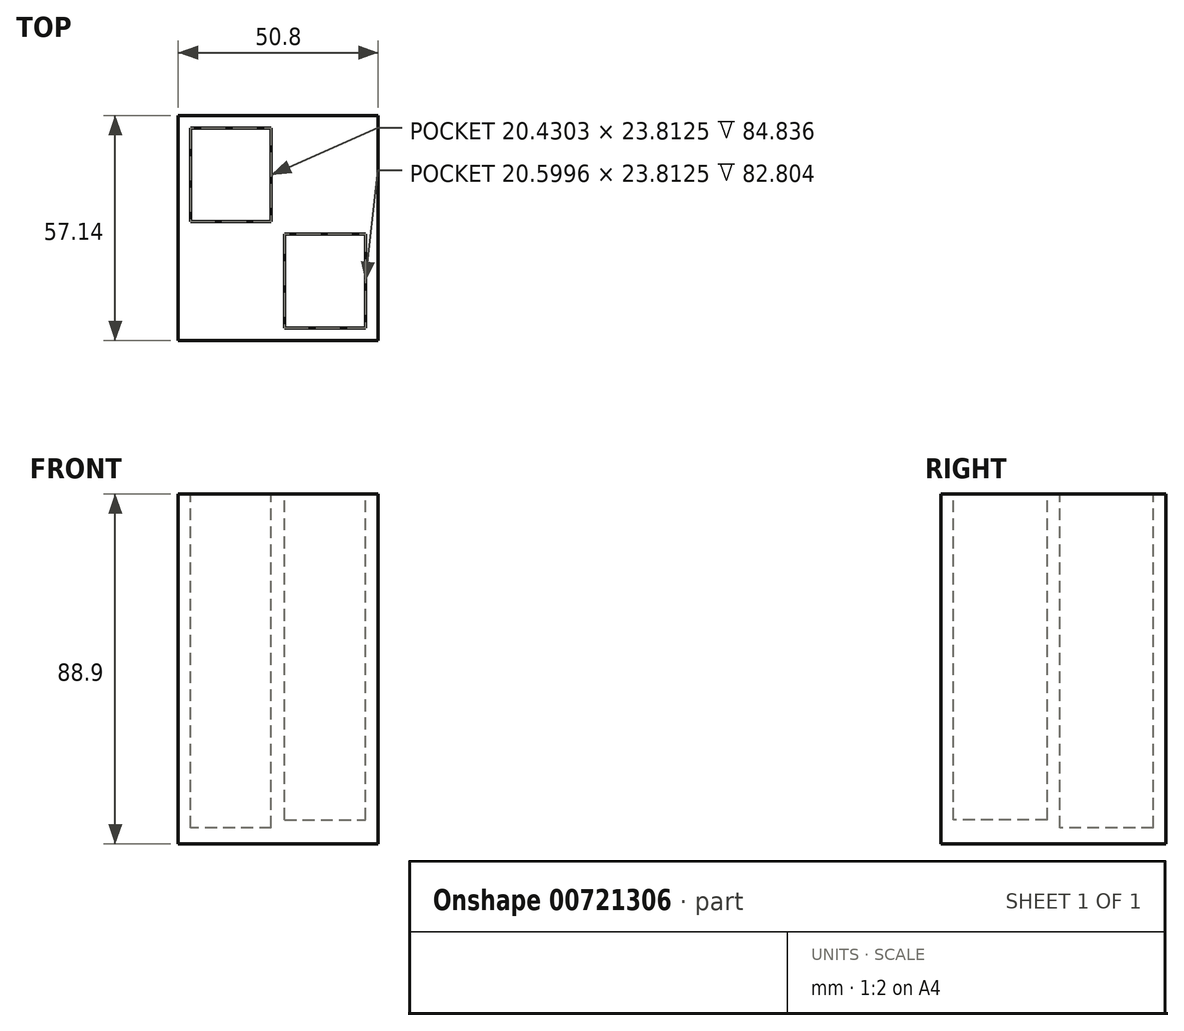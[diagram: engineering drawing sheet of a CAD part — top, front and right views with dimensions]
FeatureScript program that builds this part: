
annotation { "Feature Type Name" : "Feature", "Feature Type Description" : "" }
export const myFeature = defineFeature(function(context is Context, id is Id, definition is map)
    precondition{}
    {
        {
            var Q0;
            Q0=qCreatedBy(makeId("Top.planeOp"),FACE);
            var sketch = newSketch(context, id + "F0", { "sketchPlane" : qUnion([Q0])});
            skLineSegment(sketch, "E0.bottom", {"start": v(-25.4, 28.58) * mm, "end": v(25.4, 28.58) * mm});
            skLineSegment(sketch, "E0.top", {"start": v(-25.4, -28.58) * mm, "end": v(25.4, -28.58) * mm});
            skLineSegment(sketch, "E0.left", {"start": v(-25.4, 28.58) * mm, "end": v(-25.4, -28.58) * mm});
            skLineSegment(sketch, "E0.right", {"start": v(25.4, 28.58) * mm, "end": v(25.4, -28.58) * mm});
            skPoint(sketch, "E0.middle", {"position": v(0, 0) * mm});
            skSolve(sketch);
        }
        {
            var Q0;
            Q0 = qSketchRegion(id + "F0", true);
            extrude(context, id + "F1", {"entities" : qUnion([Q0]), "depth" : 88.9 * mm, "offsetDistance" : 25.4 * mm});
        }
        {
            var Q0;
            Q0=makeQuery(id+"F1.opExtrude","CAP_FACE",FACE,{"disambiguationData":[OSD([sQuery(id+"F0.wireOp",EDGE,"E0.bottom"),sQuery(id+"F0.wireOp",EDGE,"E0.top"),sQuery(id+"F0.wireOp",EDGE,"E0.left"),sQuery(id+"F0.wireOp",EDGE,"E0.right")])],"isStart":false});
            var sketch = newSketch(context, id + "F2", { "sketchPlane" : qUnion([Q0])});
            skLineSegment(sketch, "E1.0", {"start": v(-22.22, 25.4) * mm, "end": v(-22.23, 1.59) * mm});
            skLineSegment(sketch, "E1.1", {"start": v(22.23, 25.4) * mm, "end": v(-22.22, 25.4) * mm});
            skLineSegment(sketch, "E1.2", {"start": v(22.22, -25.4) * mm, "end": v(22.23, -1.59) * mm});
            skLineSegment(sketch, "E1.3", {"start": v(-22.23, -25.4) * mm, "end": v(22.22, -25.4) * mm});
            skLineSegment(sketch, "E2.0", {"start": v(-22.23, -1.59) * mm, "end": v(22.22, -1.59) * mm});
            skLineSegment(sketch, "E3", {"start": v(-22.23, 1.59) * mm, "end": v(22.23, 1.59) * mm});
            skPoint(sketch, "E4.orphan", {"position": v(22.23, 0) * mm});
            skLineSegment(sketch, "E5.trimOffspring", {"start": v(22.23, 1.59) * mm, "end": v(22.23, 25.4) * mm});
            skPoint(sketch, "E6.start.orphan", {"position": v(-22.23, 0) * mm});
            skLineSegment(sketch, "E7.trimOffspring", {"start": v(-22.23, -1.59) * mm, "end": v(-22.23, -25.4) * mm});
            skPoint(sketch, "E8.start.orphan", {"position": v(0, 25.4) * mm});
            skPoint(sketch, "E9.trimOffspring.end.orphan", {"position": v(0, -25.4) * mm});
            skSolve(sketch);
        }
        {
            var Q0;
            {var subQ0=sQuery(id+"F2.wireOp",EDGE,"E1.0");Q0=makeQuery(id+"F2.imprint","IMPRINT",FACE,{"disambiguationData":[TD([[makeQuery(id+"F2.imprint","IMPRINT",EDGE,{"derivedFrom":subQ0}),1.0]])]});}
            var sketch = newSketch(context, id + "F3", { "sketchPlane" : qUnion([Q0])});
            skLineSegment(sketch, "E10", {"start": v(-1.8, 25.41) * mm, "end": v(-1.8, 1.53) * mm});
            skLineSegment(sketch, "E11", {"start": v(1.44, 25.41) * mm, "end": v(1.44, 1.72) * mm});
            skSolve(sketch);
        }
        {
            var Q0;
            Q0=makeQuery(id+"F2.imprint","IMPRINT",FACE,{"disambiguationData":[TD([[makeQuery(id+"F2.imprint","IMPRINT",EDGE,{"derivedFrom":sQuery(id+"F2.wireOp",EDGE,"E1.2")}),1.0]])]});
            var sketch = newSketch(context, id + "F4", { "sketchPlane" : qUnion([Q0])});
            skLineSegment(sketch, "E12", {"start": v(-1.79, -1.63) * mm, "end": v(-1.79, -25.14) * mm});
            skPoint(sketch, "E13.start.orphan", {"position": v(0, -1.63) * mm});
            skLineSegment(sketch, "E14", {"start": v(1.63, -1.44) * mm, "end": v(1.63, -25.71) * mm});
            skSolve(sketch);
        }
        {
            var Q0;
            {var subQ5=makeQuery(id+"F2.imprint","IMPRINT",EDGE,{"derivedFrom":sQuery(id+"F2.wireOp",EDGE,"E1.0")});Q0=makeQuery(id+"F3.imprint","IMPRINT",FACE,{"disambiguationData":[TD([[makeQuery(id+"F3.imprint","IMPRINT",EDGE,{"derivedFrom":subQ5}),1.0]])]});}
            extrude(context, id + "F5", {"entities" : qUnion([Q0]), "operationType" : NewBodyOperationType.REMOVE, "oppositeDirection" : true, "depth" : 84.84 * mm, "offsetDistance" : 25.4 * mm});
        }
        {
            var Q0;
            {var subQ5=makeQuery(id+"F2.imprint","IMPRINT",EDGE,{"derivedFrom":sQuery(id+"F2.wireOp",EDGE,"E1.2")});Q0=makeQuery(id+"F4.imprint","IMPRINT",FACE,{"disambiguationData":[TD([[makeQuery(id+"F4.imprint","IMPRINT",EDGE,{"derivedFrom":subQ5}),1.0]])]});}
            extrude(context, id + "F6", {"entities" : qUnion([Q0]), "operationType" : NewBodyOperationType.REMOVE, "oppositeDirection" : true, "depth" : 82.8 * mm, "offsetDistance" : 25.4 * mm});
        }
    });
